# Revit family: VIA-Edge-Executive_Guest
name_source: partatom
category: Furniture
revit_build: Autodesk Revit 2014 (Build: 20140709_2115(x64)
units: mm (PartAtom-declared; Revit-internal decimal feet)

## types (3) — shared parameters
Assembly Code = E2020200
Caster = VIA-UHMW, Black
Depth = 2' - 4"
Glide = VIA-UHMW, Black
Height = 2' - 8"
Keynote = 12500
Legs = VIA-Aluminum
Manufacturer = VIA
Seat = VIA-Linen - Beige
Type Comments = EDGE
URL = http://www.viaseating.com
Width = 2' - 3"

## per-type parameters (varying)
| type | 4 Prong | 5 Star | Cylinder | Description | Plate |
| 985-18BA | No | Yes | No | Brushed Aluminum Star Base with Casters | No |
| 985-4POL | Yes | No | Yes | Polished 4 Leg Swivel Base with Auto-Return | No |
| 985-DISK | No | No | Yes | Brushed Disk Swivel Base with Auto-Return | Yes |

note: column(s) folded — value = type name in every type: Model

## geometry (parser evidence)
native form markers: Sweep x5
no freeform markers — native parametric forms only
